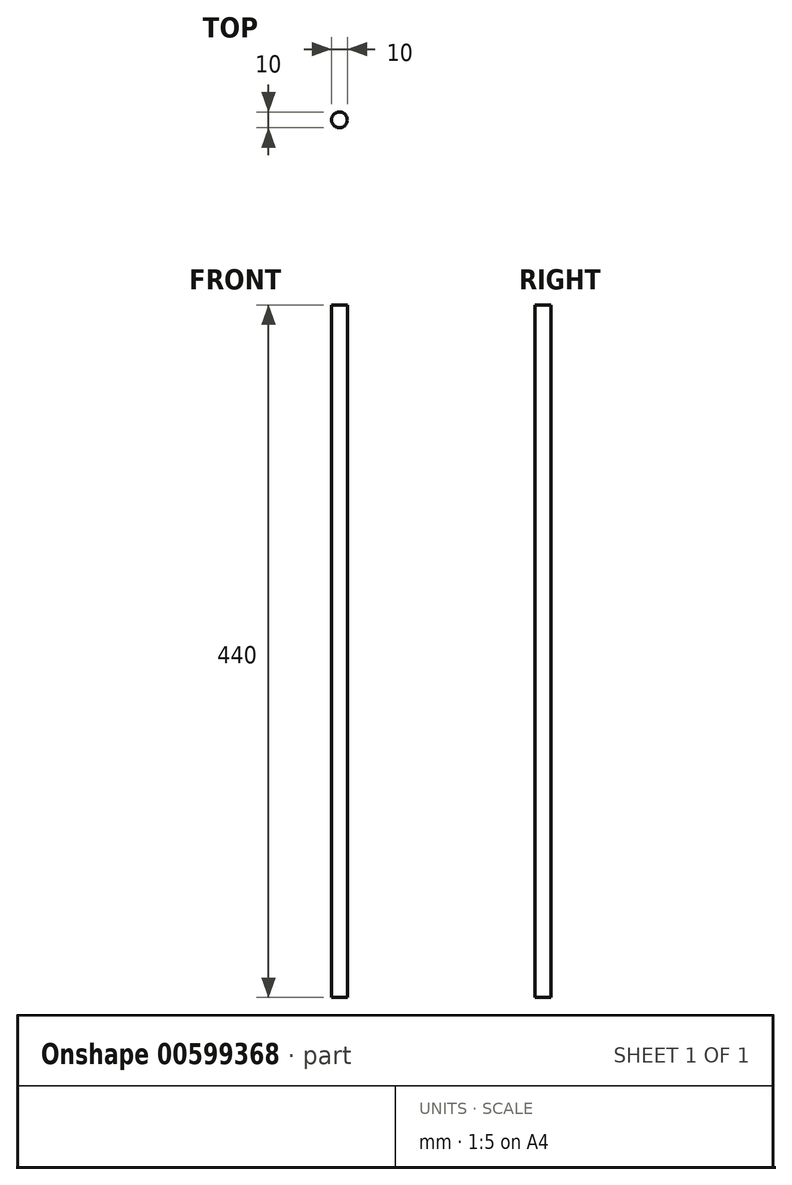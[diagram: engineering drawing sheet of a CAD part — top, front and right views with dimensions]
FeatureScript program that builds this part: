
annotation { "Feature Type Name" : "Feature", "Feature Type Description" : "" }
export const myFeature = defineFeature(function(context is Context, id is Id, definition is map)
    precondition{}
    {
        {
            var Q0;
            Q0=qCreatedBy(makeId("Top.planeOp"),FACE);
            var sketch = newSketch(context, id + "F0", { "sketchPlane" : qUnion([Q0])});
            skCircle(sketch, "E0", {"center": v(0, 0) * mm, "radius": 5 * mm});
            skSolve(sketch);
        }
        {
            var Q0;
            Q0=qSketchRegion(id+"F0",true);
            extrude(context, id + "F1", {"entities" : qUnion([Q0]), "depth" : 440 * mm, "offsetDistance" : 25 * mm});
        }
    });
